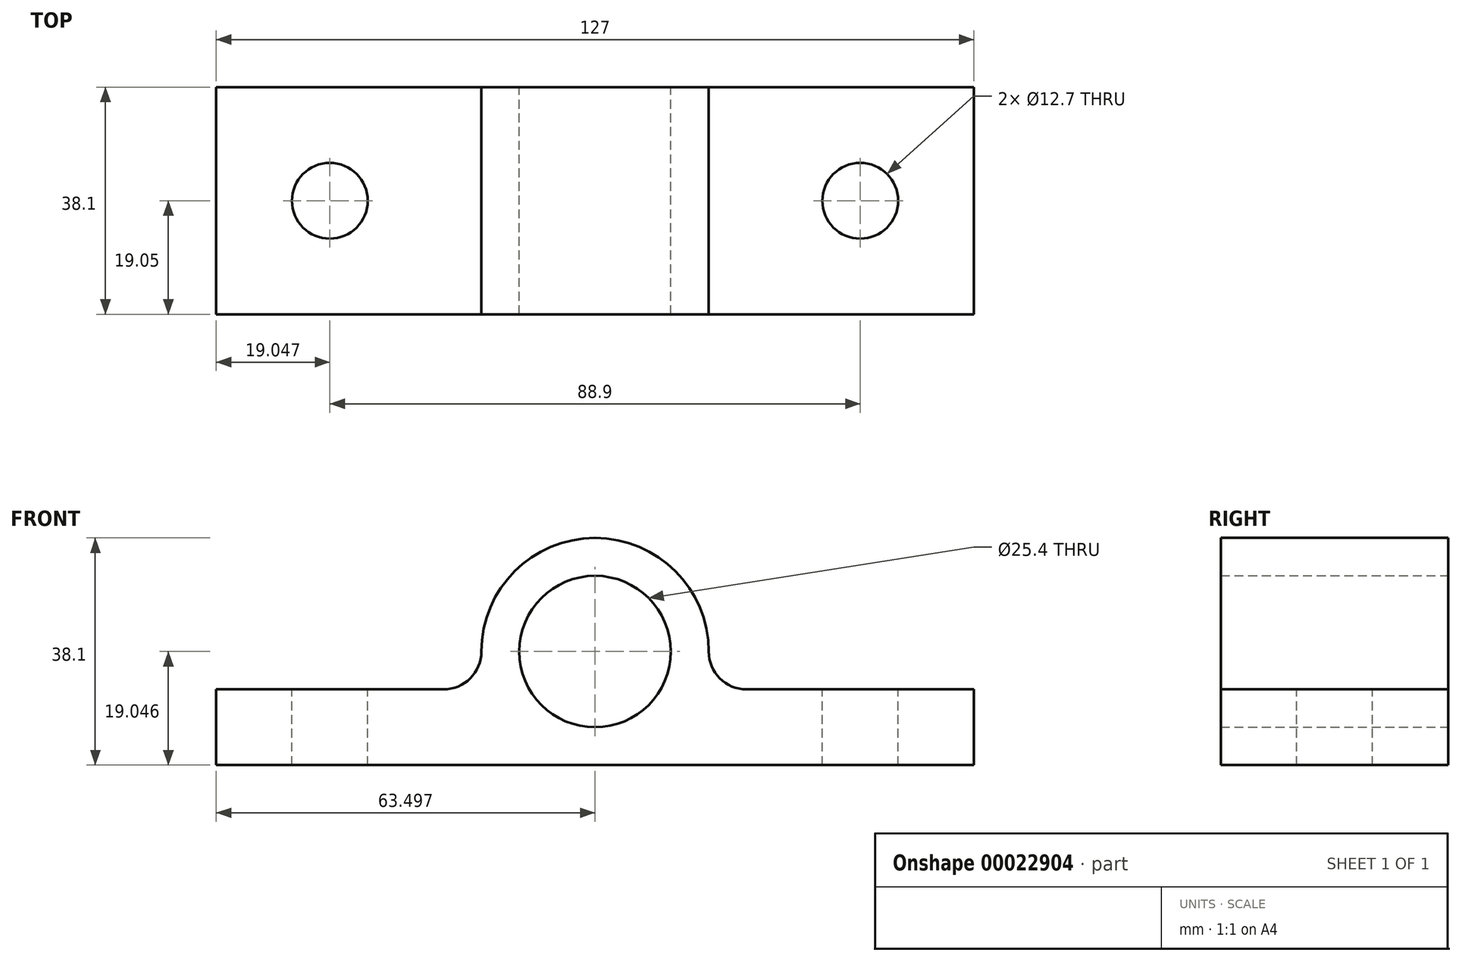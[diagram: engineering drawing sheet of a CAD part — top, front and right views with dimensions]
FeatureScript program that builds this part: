
annotation { "Feature Type Name" : "Feature", "Feature Type Description" : "" }
export const myFeature = defineFeature(function(context is Context, id is Id, definition is map)
    precondition{}
    {
        {
            var Q0;
            Q0=qCreatedBy(makeId("Front.planeOp"),FACE);
            var sketch = newSketch(context, id + "F0", { "sketchPlane" : qUnion([Q0])});
            skLineSegment(sketch, "E0.bottom", {"start": v(-32.36, 9.7) * mm, "end": v(5.74, 9.7) * mm});
            skLineSegment(sketch, "E0.top", {"start": v(-32.36, -3) * mm, "end": v(94.64, -3) * mm});
            skLineSegment(sketch, "E0.left", {"start": v(-32.36, 9.7) * mm, "end": v(-32.36, -3) * mm});
            skLineSegment(sketch, "E0.right", {"start": v(94.64, 9.7) * mm, "end": v(94.64, -3) * mm});
            skArc(sketch, "E1", {"start": v(5.74, 9.7) * mm, "mid": v(10.23, 11.57) * mm, "end": v(12.09, 16.06) * mm});
            skArc(sketch, "E2", {"start": v(50.19, 16.06) * mm, "mid": v(52.05, 11.57) * mm, "end": v(56.54, 9.7) * mm});
            skArc(sketch, "E3", {"start": v(50.19, 16.06) * mm, "mid": v(31.14, 35.1) * mm, "end": v(12.09, 16.06) * mm});
            skCircle(sketch, "E4", {"center": v(31.14, 16.06) * mm, "radius": 12.7 * mm});
            skPoint(sketch, "E5.orphan", {"position": v(31.14, -3) * mm});
            skPoint(sketch, "E6.start.orphan", {"position": v(31.14, 9.7) * mm});
            skLineSegment(sketch, "E7.trimOffspring", {"start": v(56.54, 9.7) * mm, "end": v(94.64, 9.7) * mm});
            skSolve(sketch);
        }
        {
            var Q0;
            Q0 = qSketchRegion(id + "F0", true);
            extrude(context, id + "F1", {"entities" : qUnion([Q0]), "depth" : 38.1 * mm});
        }
        {
            var Q0;
            Q0=makeQuery(id+"F1.opExtrude","SWEPT_FACE",FACE,{"disambiguationData":[OSD([sQuery(id+"F0.wireOp",EDGE,"E0.bottom")])]});
            var sketch = newSketch(context, id + "F2", { "sketchPlane" : qUnion([Q0])});
            skCircle(sketch, "E8", {"center": v(75.59, -19.05) * mm, "radius": 6.35 * mm});
            skCircle(sketch, "E9", {"center": v(-13.31, -19.05) * mm, "radius": 6.35 * mm});
            skSolve(sketch);
        }
        {
            var Q0;
            Q0 = qSketchRegion(id + "F2", true);
            extrude(context, id + "F3", {"entities" : qUnion([Q0]), "operationType" : NewBodyOperationType.REMOVE, "oppositeDirection" : true, "depth" : 25.4 * mm});
        }
    });
